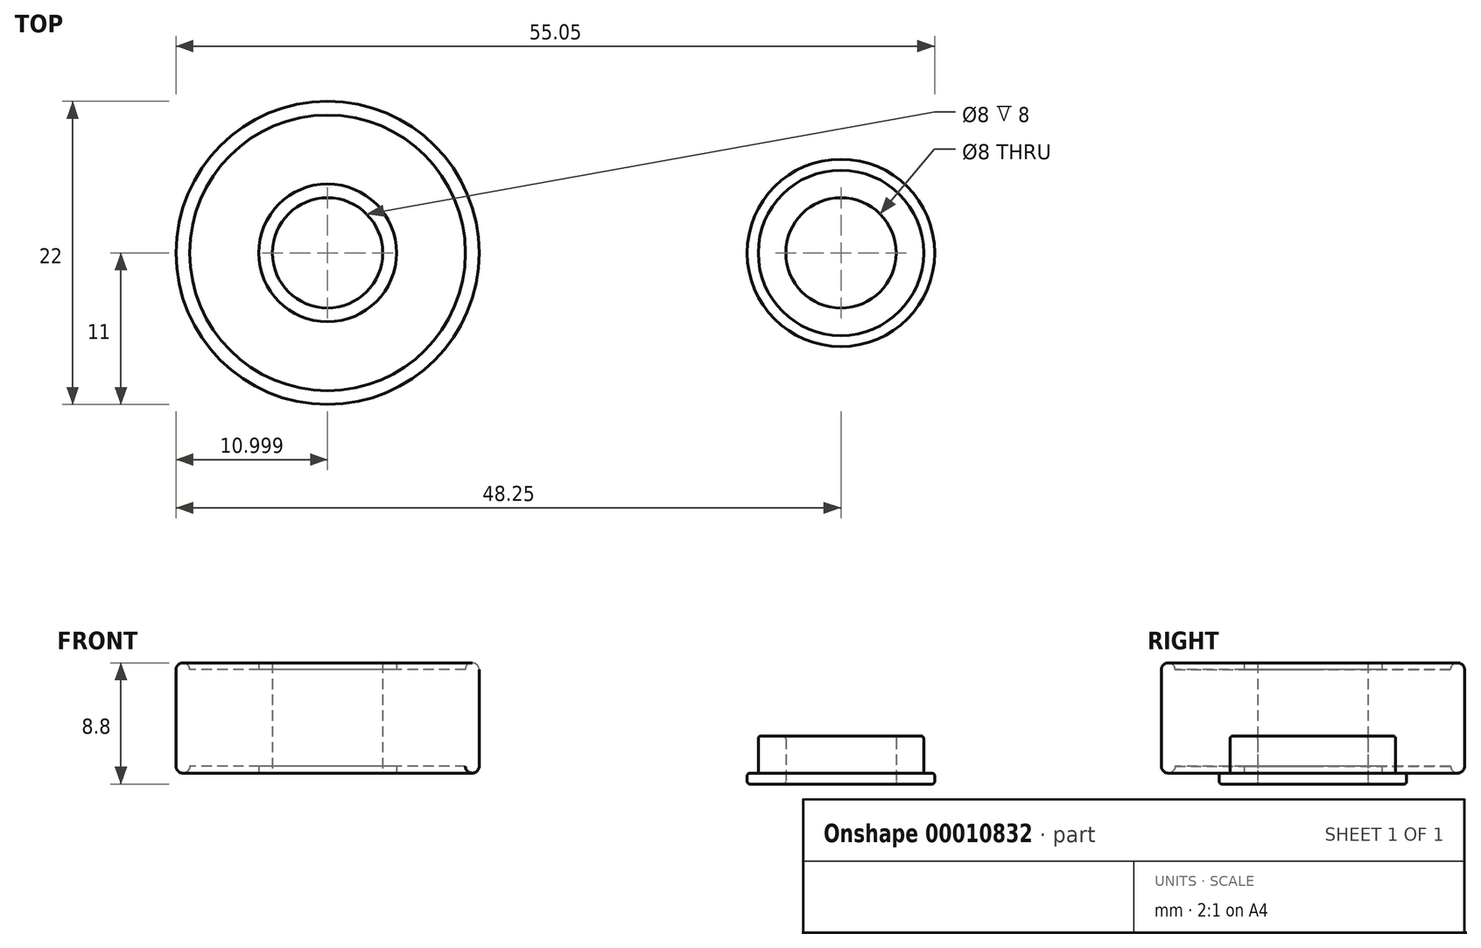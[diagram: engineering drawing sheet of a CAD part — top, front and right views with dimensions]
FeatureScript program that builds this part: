
annotation { "Feature Type Name" : "Feature", "Feature Type Description" : "" }
export const myFeature = defineFeature(function(context is Context, id is Id, definition is map)
    precondition{}
    {
        {
            var Q0;
            Q0=qCreatedBy(makeId("Top.planeOp"),FACE);
            var sketch = newSketch(context, id + "F0", { "sketchPlane" : qUnion([Q0])});
            skCircle(sketch, "E0", {"center": v(0, 0) * mm, "radius": 4 * mm});
            skCircle(sketch, "E1", {"center": v(0, 0) * mm, "radius": 6 * mm});
            skCircle(sketch, "E2", {"center": v(0, 0) * mm, "radius": 6.8 * mm});
            skCircle(sketch, "E3", {"center": v(-37.25, 0) * mm, "radius": 4 * mm});
            skCircle(sketch, "E4", {"center": v(-37.25, 0) * mm, "radius": 5 * mm});
            skCircle(sketch, "E5", {"center": v(-37.25, 0) * mm, "radius": 10 * mm});
            skCircle(sketch, "E6", {"center": v(-37.25, 0) * mm, "radius": 11 * mm});
            skSolve(sketch);
        }
        {
            var Q0;
            Q0=makeQuery(id+"F0.imprint","IMPRINT",FACE,{"disambiguationData":[TD([[makeQuery(id+"F0.imprint","IMPRINT",EDGE,{"derivedFrom":sQuery(id+"F0.wireOp",EDGE,"E0")}),-1.0]])]});
            extrude(context, id + "F1", {"entities" : qUnion([Q0]), "depth" : 2.7 * mm});
        }
        {
            var Q0;
            Q0=makeQuery(id+"F0.imprint","IMPRINT",FACE,{"disambiguationData":[TD([[makeQuery(id+"F0.imprint","IMPRINT",EDGE,{"derivedFrom":sQuery(id+"F0.wireOp",EDGE,"E0")}),-1.0]])]});
            var Q1;
            Q1=makeQuery(id+"F0.imprint","IMPRINT",FACE,{"disambiguationData":[TD([[makeQuery(id+"F0.imprint","IMPRINT",EDGE,{"derivedFrom":sQuery(id+"F0.wireOp",EDGE,"E1")}),-1.0]])]});
            extrude(context, id + "F2", {"entities" : qUnion([Q0, Q1]), "operationType" : NewBodyOperationType.ADD, "oppositeDirection" : true, "depth" : 0.8 * mm});
        }
        {
            var Q0;
            Q0=makeQuery(id+"F1.opExtrude","CAP_EDGE",EDGE,{"disambiguationData":[OSD([sQuery(id+"F0.wireOp",EDGE,"E1")])],"isStart":false});
            var Q1;
            Q1=makeQuery(id+"F2.opExtrude","CAP_EDGE",EDGE,{"disambiguationData":[OSD([sQuery(id+"F0.wireOp",EDGE,"E2")])],"isStart":true});
            var Q2;
            Q2=makeQuery(id+"F2.opExtrude","CAP_EDGE",EDGE,{"disambiguationData":[OSD([sQuery(id+"F0.wireOp",EDGE,"E2")])],"isStart":false});
            var Q3;
            Q3=makeQuery(id+"F1.opExtrude","CAP_EDGE",EDGE,{"disambiguationData":[OSD([sQuery(id+"F0.wireOp",EDGE,"E1")])],"isStart":true});
            var Q4;
            Q4=makeQuery(id+"F1.opExtrude","CAP_EDGE",EDGE,{"disambiguationData":[OSD([sQuery(id+"F0.wireOp",EDGE,"E0")])],"isStart":false});
            var Q5;
            Q5=makeQuery(id+"F2.opExtrude","CAP_EDGE",EDGE,{"disambiguationData":[OSD([sQuery(id+"F0.wireOp",EDGE,"E0")])],"isStart":false});
            fillet(context, id + "F3", {"entities" : qUnion([Q0, Q1, Q2, Q3, Q4, Q5]), "radius" : 0.2 * mm, "tangentPropagation" : true, "allowEdgeOverflow" : false});
        }
        {
            var Q0;
            Q0=makeQuery(id+"F0.imprint","IMPRINT",FACE,{"disambiguationData":[TD([[makeQuery(id+"F0.imprint","IMPRINT",EDGE,{"derivedFrom":sQuery(id+"F0.wireOp",EDGE,"E5")}),-1.0]])]});
            var Q1;
            Q1=makeQuery(id+"F0.imprint","IMPRINT",FACE,{"disambiguationData":[TD([[makeQuery(id+"F0.imprint","IMPRINT",EDGE,{"derivedFrom":sQuery(id+"F0.wireOp",EDGE,"E3")}),-1.0]])]});
            extrude(context, id + "F4", {"entities" : qUnion([Q0, Q1]), "depth" : 8 * mm});
        }
        {
            var Q0;
            Q0=makeQuery(id+"F0.imprint","IMPRINT",FACE,{"disambiguationData":[TD([[makeQuery(id+"F0.imprint","IMPRINT",EDGE,{"derivedFrom":sQuery(id+"F0.wireOp",EDGE,"E4")}),-1.0]])]});
            extrude(context, id + "F5", {"entities" : qUnion([Q0]), "operationType" : NewBodyOperationType.ADD, "depth" : 7.5 * mm, "hasSecondDirection" : true, "secondDirectionOppositeDirection" : false, "secondDirectionDepth" : 0.5 * mm});
        }
        {
            var Q0;
            Q0=makeQuery(id+"F4.opExtrude","CAP_FACE",FACE,{"disambiguationData":[OSD([sQuery(id+"F0.wireOp",EDGE,"E5"),sQuery(id+"F0.wireOp",EDGE,"E6")])],"isStart":false});
            var Q1;
            Q1=makeQuery(id+"F4.opExtrude","CAP_FACE",FACE,{"disambiguationData":[OSD([sQuery(id+"F0.wireOp",EDGE,"E5"),sQuery(id+"F0.wireOp",EDGE,"E6")])],"isStart":true});
            fillet(context, id + "F6", {"entities" : qUnion([Q0, Q1]), "radius" : 0.5 * mm, "tangentPropagation" : true, "allowEdgeOverflow" : false});
        }
    });
